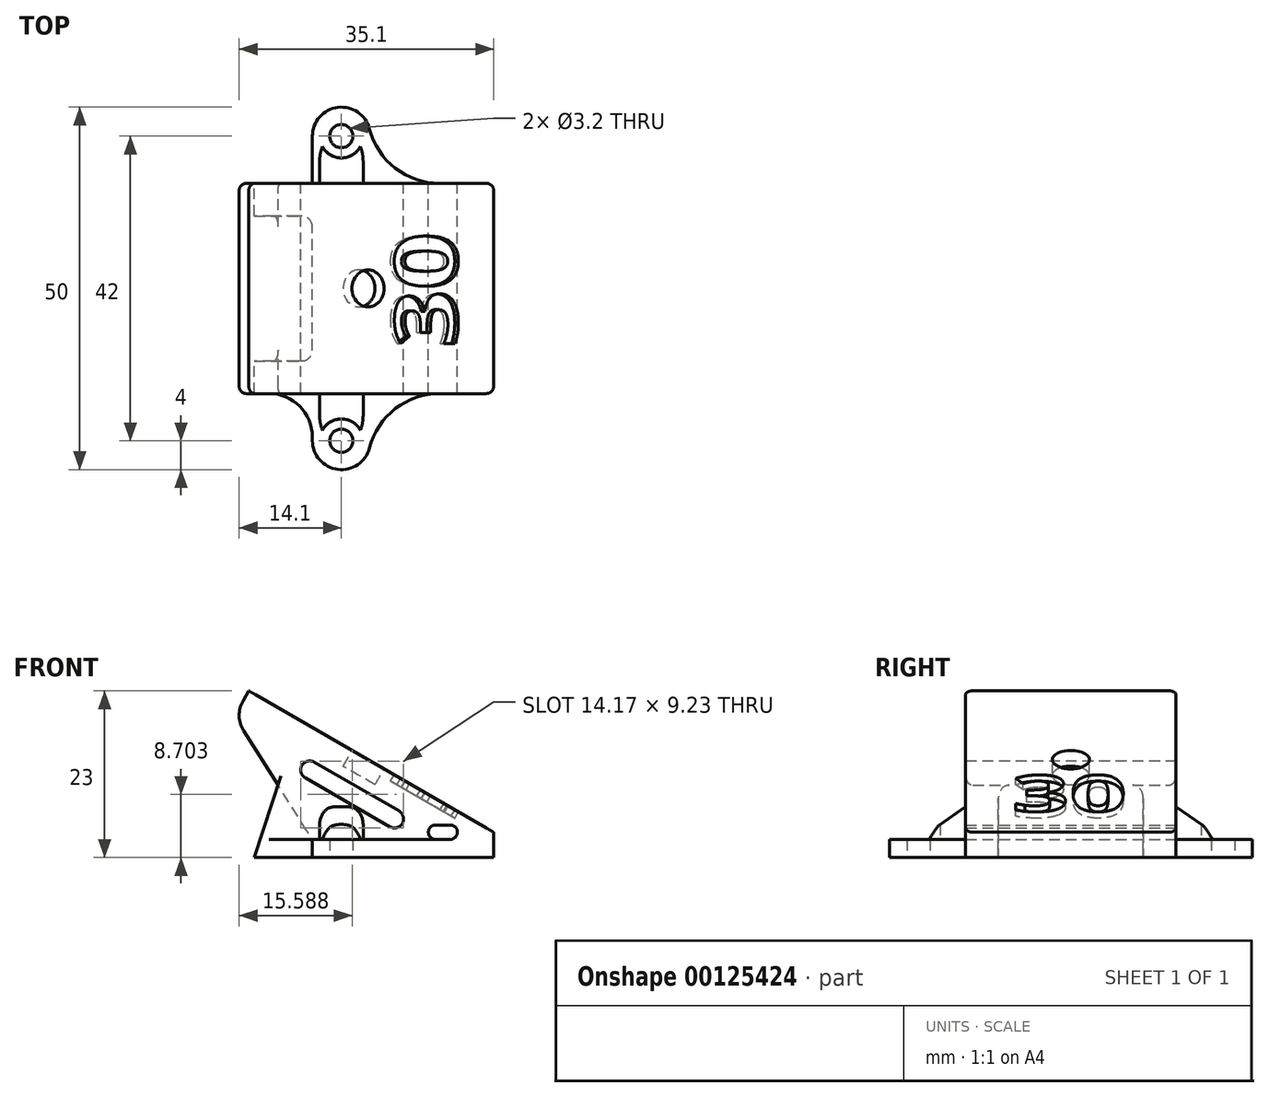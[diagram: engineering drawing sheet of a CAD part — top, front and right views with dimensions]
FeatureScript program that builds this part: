
annotation { "Feature Type Name" : "Feature", "Feature Type Description" : "" }
export const myFeature = defineFeature(function(context is Context, id is Id, definition is map)
    precondition{}
    {
        {
            var Q0;
            Q0=qCreatedBy(makeId("Front.planeOp"),FACE);
            var sketch = newSketch(context, id + "F0", { "sketchPlane" : qUnion([Q0])});
            skLineSegment(sketch, "E0", {"start": v(-33.77, 23) * mm, "end": v(0, 3.5) * mm});
            skLineSegment(sketch, "E1", {"start": v(-33.77, 23) * mm, "end": v(-34.57, 21.63) * mm});
            skLineSegment(sketch, "E2", {"start": v(-34.48, 17.5) * mm, "end": v(-25, 2.5) * mm});
            skLineSegment(sketch, "E3", {"start": v(0, 0) * mm, "end": v(0, 3.5) * mm});
            skLineSegment(sketch, "E4", {"start": v(-26.44, 12.7) * mm, "end": v(-26.44, 12.7) * mm});
            skLineSegment(sketch, "E5", {"start": v(-25.98, 11) * mm, "end": v(-14.3, 4.25) * mm});
            skLineSegment(sketch, "E6", {"start": v(-12.58, 4.7) * mm, "end": v(-12.58, 4.7) * mm});
            skLineSegment(sketch, "E7", {"start": v(-13.04, 6.41) * mm, "end": v(-24.73, 13.16) * mm});
            skLineSegment(sketch, "E8", {"start": v(-16.89, 13.25) * mm, "end": v(-18.89, 9.79) * mm, "construction": true});
            skPoint(sketch, "E9.visualSharp", {"position": v(-25.82, 13.79) * mm});
            skArc(sketch, "E9.filletArc", {"start": v(-24.73, 13.16) * mm, "mid": v(-25.68, 13.29) * mm, "end": v(-26.44, 12.7) * mm});
            skPoint(sketch, "E10.visualSharp", {"position": v(-11.96, 5.79) * mm});
            skArc(sketch, "E10.filletArc", {"start": v(-12.58, 4.7) * mm, "mid": v(-12.46, 5.65) * mm, "end": v(-13.04, 6.41) * mm});
            skPoint(sketch, "E11.visualSharp", {"position": v(-13.2, 3.62) * mm});
            skArc(sketch, "E11.filletArc", {"start": v(-14.3, 4.25) * mm, "mid": v(-13.34, 4.12) * mm, "end": v(-12.58, 4.7) * mm});
            skPoint(sketch, "E12.visualSharp", {"position": v(-27.07, 11.62) * mm});
            skArc(sketch, "E12.filletArc", {"start": v(-26.44, 12.7) * mm, "mid": v(-26.57, 11.75) * mm, "end": v(-25.98, 11) * mm});
            skLineSegment(sketch, "E13", {"start": v(-8, 3.5) * mm, "end": v(-6, 3.5) * mm, "construction": true});
            skArc(sketch, "E14.0.startCap", {"start": v(-8, 2.5) * mm, "mid": v(-9, 3.5) * mm, "end": v(-8, 4.5) * mm});
            skArc(sketch, "E14.0.endCap", {"start": v(-6, 4.5) * mm, "mid": v(-5, 3.5) * mm, "end": v(-6, 2.5) * mm});
            skLineSegment(sketch, "E14.0.left", {"start": v(-8, 4.5) * mm, "end": v(-6, 4.5) * mm});
            skLineSegment(sketch, "E14.0.right", {"start": v(-8, 2.5) * mm, "end": v(-6, 2.5) * mm});
            skPoint(sketch, "E15.visualSharp", {"position": v(-35.77, 19.54) * mm});
            skArc(sketch, "E15.filletArc", {"start": v(-34.57, 21.63) * mm, "mid": v(-35.1, 19.55) * mm, "end": v(-34.48, 17.5) * mm});
            skLineSegment(sketch, "E16", {"start": v(0, 0) * mm, "end": v(-25, 0) * mm});
            skLineSegment(sketch, "E17", {"start": v(-25, 2.5) * mm, "end": v(-25, 0) * mm});
            skSolve(sketch);
        }
        {
            var Q0;
            Q0=makeQuery(id+"F0.imprint","IMPRINT",FACE,{"disambiguationData":[TD([[makeQuery(id+"F0.imprint","IMPRINT",EDGE,{"derivedFrom":sQuery(id+"F0.wireOp",EDGE,"E0")}),-1.0]])]});
            extrude(context, id + "F1", {"entities" : qUnion([Q0]), "endBound" : BoundingType.SYMMETRIC, "depth" : 29 * mm, "offsetDistance" : 25 * mm});
        }
        {
            var Q0;
            Q0=makeQuery(id+"F1.opExtrude","SWEPT_FACE",FACE,{"disambiguationData":[OSD([sQuery(id+"F0.wireOp",EDGE,"E16")])]});
            var sketch = newSketch(context, id + "F2", { "sketchPlane" : qUnion([Q0])});
            skCircle(sketch, "E18", {"center": v(-21, 21) * mm, "radius": 1.6 * mm});
            skArc(sketch, "E19", {"start": v(-17.13, 22) * mm, "mid": v(-21.5, 24.97) * mm, "end": v(-25, 21) * mm});
            skCircle(sketch, "E20.MirrorC", {"center": v(-21, -21) * mm, "radius": 1.6 * mm});
            skLineSegment(sketch, "E21", {"start": v(-25, 21) * mm, "end": v(-25, -21) * mm});
            skArc(sketch, "E22", {"start": v(-17.13, 22) * mm, "mid": v(-13.57, 16.6) * mm, "end": v(-7.44, 14.5) * mm});
            skLineSegment(sketch, "E23", {"start": v(-7.44, 14.5) * mm, "end": v(-7.44, -14.5) * mm});
            skArc(sketch, "E24.MirrorCS", {"start": v(-17.13, -22) * mm, "mid": v(-21.5, -24.97) * mm, "end": v(-25, -21) * mm});
            skArc(sketch, "E25.MirrorCS", {"start": v(-17.13, -22) * mm, "mid": v(-13.57, -16.6) * mm, "end": v(-7.44, -14.5) * mm});
            skSolve(sketch);
        }
        {
            var Q0;
            Q0=qSketchRegion(id+"F2",true);
            extrude(context, id + "F3", {"entities" : qUnion([Q0]), "operationType" : NewBodyOperationType.ADD, "oppositeDirection" : true, "depth" : 2.5 * mm, "offsetDistance" : 25 * mm});
        }
        {
            var Q0;
            {var subQ4=sQuery(id+"F2.wireOp",EDGE,"E21");var subQ6=sQuery(id+"F2.wireOp",EDGE,"E19");Q0=makeQuery(id+"Fg2Gqv11Pvh0zDd_1.boolean.opBoolean","SPLIT",FACE,{"disambiguationData":[TD([makeQuery(id+"F3.opExtrude","SWEPT_FACE",FACE,{"disambiguationData":[OSD([subQ6])]})])],"derivedFrom":makeQuery(id+"F3.boolean.opBoolean","MERGE",FACE,{"derivedFrom":[makeQuery(id+"F1.opExtrude","SWEPT_FACE",FACE,{"disambiguationData":[OSD([sQuery(id+"F0.wireOp",EDGE,"E17")])]}),makeQuery(id+"F3.opExtrude","SWEPT_FACE",FACE,{"disambiguationData":[OSD([subQ4])]})]})});}
            var sketch = newSketch(context, id + "F4", { "sketchPlane" : qUnion([Q0])});
            skLineSegment(sketch, "E26", {"start": v(-21, 2.5) * mm, "end": v(-14.5, 7) * mm});
            skLineSegment(sketch, "E27", {"start": v(-14.5, 7) * mm, "end": v(-14.5, 2.5) * mm});
            skLineSegment(sketch, "E28", {"start": v(-14.5, 2.5) * mm, "end": v(-21, 2.5) * mm});
            skSolve(sketch);
        }
        {
            var Q0;
            Q0=makeQuery(id+"F4.imprint","IMPRINT",FACE,{"disambiguationData":[TD([[makeQuery(id+"F4.imprint","IMPRINT",EDGE,{"derivedFrom":sQuery(id+"F4.wireOp",EDGE,"E26")}),-1.0]])]});
            extrude(context, id + "F5", {"entities" : qUnion([Q0]), "oppositeDirection" : true, "depth" : 7 * mm, "offsetDistance" : 25 * mm, "hasSecondDirection" : true, "secondDirectionOppositeDirection" : true, "secondDirectionDepth" : 1 * mm});
        }
        {
            var Q0;
            Q0=makeQuery(id+"F5.opExtrude","SWEPT_BODY",BODY,{"disambiguationData":[OSD([sQuery(id+"F4.wireOp",EDGE,"E26"),sQuery(id+"F4.wireOp",EDGE,"E27"),sQuery(id+"F4.wireOp",EDGE,"E28")])]});
            var Q1;
            Q1=qCreatedBy(makeId("Front.planeOp"),FACE);
            mirror(context, id + "F6", {"operationType" : NewBodyOperationType.ADD, "entities" : qUnion([Q0]), "mirrorPlane" : qUnion([Q1])});
        }
        {
            var Q0;
            {var subQ0=sQuery(id+"F2.wireOp",EDGE,"E20.MirrorC");var subQ2=sQuery(id+"F2.wireOp",EDGE,"E21");var subQ4=sQuery(id+"F2.wireOp",EDGE,"E24.MirrorCS");var subQ5=sQuery(id+"F2.wireOp",EDGE,"E25.MirrorCS");Q0=makeQuery(id+"F3.boolean.opBoolean","SPLIT",FACE,{"disambiguationData":[TD([makeQuery(id+"F3.opExtrude","SWEPT_FACE",FACE,{"disambiguationData":[OSD([subQ0])]})])],"derivedFrom":makeQuery(id+"F3.opExtrude","CAP_FACE",FACE,{"disambiguationData":[OSD([sQuery(id+"F2.wireOp",EDGE,"E18"),sQuery(id+"F2.wireOp",EDGE,"E19"),subQ0,subQ2,sQuery(id+"F2.wireOp",EDGE,"E22"),sQuery(id+"F2.wireOp",EDGE,"E23"),subQ4,subQ5])],"isStart":false})});}
            var sketch = newSketch(context, id + "F7", { "sketchPlane" : qUnion([Q0])});
            skCircle(sketch, "E29", {"center": v(-21, 21) * mm, "radius": 3 * mm});
            skCircle(sketch, "E30", {"center": v(-21, -21) * mm, "radius": 3 * mm});
            skSolve(sketch);
        }
        {
            var Q0;
            Q0=makeQuery(id+"F5.opExtrude","CAP_EDGE",EDGE,{"disambiguationData":[OSD([sQuery(id+"F4.wireOp",EDGE,"E26")])],"isStart":true});
            var Q1;
            Q1=makeQuery(id+"F5.opExtrude","CAP_EDGE",EDGE,{"disambiguationData":[OSD([sQuery(id+"F4.wireOp",EDGE,"E26")])],"isStart":false});
            var Q2;
            Q2=makeQuery(id+"F6.opPattern","COPY",EDGE,{"derivedFrom":makeQuery(id+"F5.opExtrude","CAP_EDGE",EDGE,{"disambiguationData":[OSD([sQuery(id+"F4.wireOp",EDGE,"E26")])],"isStart":true}),"instanceName":"1"});
            var Q3;
            Q3=makeQuery(id+"F6.opPattern","COPY",EDGE,{"derivedFrom":makeQuery(id+"F5.opExtrude","CAP_EDGE",EDGE,{"disambiguationData":[OSD([sQuery(id+"F4.wireOp",EDGE,"E26")])],"isStart":false}),"instanceName":"1"});
            fillet(context, id + "F8", {"entities" : qUnion([Q0, Q1, Q2, Q3]), "radius" : 2 * mm, "tangentPropagation" : true, "allowEdgeOverflow" : false});
        }
        {
            var Q0;
            Q0=qSketchRegion(id+"F7",true);
            extrude(context, id + "F9", {"entities" : qUnion([Q0]), "operationType" : NewBodyOperationType.REMOVE, "depth" : 25 * mm, "offsetDistance" : 25 * mm});
        }
        {
            var Q0;
            Q0=makeQuery(id+"F1.opExtrude","SWEPT_FACE",FACE,{"disambiguationData":[OSD([sQuery(id+"F0.wireOp",EDGE,"E0")])]});
            var sketch = newSketch(context, id + "F10", { "sketchPlane" : qUnion([Q0])});
            skCircle(sketch, "E31", {"center": v(-21.75, 0) * mm, "radius": 2.55 * mm});
            skLineSegment(sketch, "E32", {"start": v(-21.75, 0) * mm, "end": v(0, 0) * mm, "construction": true});
            skText(sketch, "E33", { "text": "30", "fontName": "OpenSans-Bold.ttf"});
            const initialGuessF10  = {"E33": [-0.0075, -0.00813, 0, 1, 0.01]};
            skSetInitialGuess(sketch, initialGuessF10);
            skSolve(sketch);
        }
        {
            var Q0;
            Q0=makeQuery(id+"F10.imprint","IMPRINT",FACE,{"disambiguationData":[TD([[makeQuery(id+"F10.imprint","IMPRINT",EDGE,{"derivedFrom":sQuery(id+"F10.wireOp",EDGE,"E31")}),1.0]])]});
            extrude(context, id + "F11", {"entities" : qUnion([Q0]), "operationType" : NewBodyOperationType.REMOVE, "depth" : -2.5 * mm, "offsetDistance" : 25 * mm});
        }
        {
            var Q0;
            Q0=makeQuery(id+"F10.imprint","IMPRINT",FACE,{"disambiguationData":[TD([[makeQuery(id+"F10.imprint","IMPRINT",EDGE,{"derivedFrom":sQuery(id+"F10.wireOp",EDGE,"E33.sketch_text.stroke-0")}),-1.0]])]});
            var Q1;
            Q1=makeQuery(id+"F10.imprint","IMPRINT",FACE,{"disambiguationData":[TD([[makeQuery(id+"F10.imprint","IMPRINT",EDGE,{"derivedFrom":sQuery(id+"F10.wireOp",EDGE,"E33.sketch_text.stroke-27")}),-1.0]])]});
            extrude(context, id + "F12", {"entities" : qUnion([Q0, Q1]), "operationType" : NewBodyOperationType.REMOVE, "oppositeDirection" : true, "depth" : 1 * mm, "offsetDistance" : 25 * mm});
        }
        {
            var Q0;
            Q0=qCreatedBy(makeId("Front.planeOp"),FACE);
            var sketch = newSketch(context, id + "F13", { "sketchPlane" : qUnion([Q0])});
            skLineSegment(sketch, "E34", {"start": v(-29.74, 10) * mm, "end": v(-33, 0) * mm});
            skLineSegment(sketch, "E35", {"start": v(-33, 0) * mm, "end": v(-25, 0) * mm});
            skLineSegment(sketch, "E36", {"start": v(-25, 0) * mm, "end": v(-25, 2.5) * mm});
            skLineSegment(sketch, "E37", {"start": v(-25, 2.5) * mm, "end": v(-29.74, 10) * mm});
            skSolve(sketch);
        }
        {
            var Q0;
            Q0=makeQuery(id+"F13.imprint","IMPRINT",FACE,{"disambiguationData":[TD([[makeQuery(id+"F13.imprint","IMPRINT",EDGE,{"derivedFrom":sQuery(id+"F13.wireOp",EDGE,"E34")}),1.0]])]});
            extrude(context, id + "F14", {"entities" : qUnion([Q0]), "operationType" : NewBodyOperationType.ADD, "endBound" : BoundingType.SYMMETRIC, "depth" : 29 * mm, "offsetDistance" : 25 * mm});
        }
        {
            var Q0;
            Q0 = qSketchRegion(id + "F13", true);
            extrude(context, id + "F15", {"entities" : qUnion([Q0]), "operationType" : NewBodyOperationType.REMOVE, "endBound" : BoundingType.SYMMETRIC, "depth" : 20 * mm, "offsetDistance" : 25 * mm});
        }
        {
            var Q0;
            Q0=makeQuery(id+"F15.boolean.opBoolean","COPY",EDGE,{"derivedFrom":makeQuery(id+"F15.opExtrude","SWEPT_EDGE",EDGE,{"disambiguationData":[OSD([sQuery(id+"F13.wireOp",EDGE,"E36"),sQuery(id+"F13.wireOp",EDGE,"E37")])]})});
            var Q1;
            {var subQ0=sQuery(id+"F13.wireOp",EDGE,"E37");var subQ1=sQuery(id+"F13.wireOp",EDGE,"E36");var subQ2=sQuery(id+"F13.wireOp",EDGE,"E35");var subQ3=sQuery(id+"F13.wireOp",EDGE,"E34");Q1=makeQuery(id+"F15.boolean.opBoolean","SPLIT",EDGE,{"disambiguationData":[TD([makeQuery(id+"F14.opExtrude","CAP_FACE",FACE,{"disambiguationData":[OSD([subQ3,subQ2,subQ1,subQ0])],"isStart":true})])],"derivedFrom":makeQuery(id+"F14.opExtrude","SWEPT_EDGE",EDGE,{"disambiguationData":[OSD([subQ3,subQ0])]})});}
            var Q2;
            {var subQ0=sQuery(id+"F13.wireOp",EDGE,"E37");var subQ1=sQuery(id+"F13.wireOp",EDGE,"E36");var subQ2=sQuery(id+"F13.wireOp",EDGE,"E35");var subQ3=sQuery(id+"F13.wireOp",EDGE,"E34");Q2=makeQuery(id+"F15.boolean.opBoolean","SPLIT",EDGE,{"disambiguationData":[TD([makeQuery(id+"F14.opExtrude","CAP_FACE",FACE,{"disambiguationData":[OSD([subQ3,subQ2,subQ1,subQ0])],"isStart":false})])],"derivedFrom":makeQuery(id+"F14.opExtrude","SWEPT_EDGE",EDGE,{"disambiguationData":[OSD([subQ3,subQ0])]})});}
            fillet(context, id + "F16", {"entities" : qUnion([Q0, Q1, Q2]), "radius" : 5 * mm, "tangentPropagation" : true, "allowEdgeOverflow" : false});
        }
        {
            var Q0;
            Q0=makeQuery(id+"F15.boolean.opBoolean","COPY",EDGE,{"derivedFrom":makeQuery(id+"F15.opExtrude","CAP_EDGE",EDGE,{"disambiguationData":[OSD([sQuery(id+"F13.wireOp",EDGE,"E37")])],"isStart":true})});
            var Q1;
            Q1=makeQuery(id+"F15.boolean.opBoolean","COPY",EDGE,{"derivedFrom":makeQuery(id+"F15.opExtrude","CAP_EDGE",EDGE,{"disambiguationData":[OSD([sQuery(id+"F13.wireOp",EDGE,"E37")])],"isStart":false})});
            fillet(context, id + "F17", {"entities" : qUnion([Q0, Q1]), "radius" : 1.5 * mm, "tangentPropagation" : true, "allowEdgeOverflow" : false});
        }
        {
            var Q0;
            Q0=makeQuery(id+"F1.opExtrude","CAP_EDGE",EDGE,{"disambiguationData":[OSD([sQuery(id+"F0.wireOp",EDGE,"E1")])],"isStart":true});
            var Q1;
            Q1=makeQuery(id+"F1.opExtrude","CAP_EDGE",EDGE,{"disambiguationData":[OSD([sQuery(id+"F0.wireOp",EDGE,"E1")])],"isStart":false});
            var Q2;
            {var subQ0=sQuery(id+"F13.wireOp",EDGE,"E37");var subQ1=sQuery(id+"F13.wireOp",EDGE,"E36");var subQ2=sQuery(id+"F13.wireOp",EDGE,"E35");var subQ3=sQuery(id+"F13.wireOp",EDGE,"E34");Q2=makeQuery(id+"F17.opFillet","BLEND_EDGE",EDGE,{"blendedFrom":[makeQuery(id+"F15.boolean.opBoolean","COPY",EDGE,{"derivedFrom":makeQuery(id+"F15.opExtrude","CAP_EDGE",EDGE,{"disambiguationData":[OSD([subQ0])],"isStart":false})}),makeQuery(id+"F16.opFillet","BLEND_FACE",FACE,{"disambiguationData":[OSD([subQ3,subQ0]),TDD([makeQuery(id+"F15.boolean.opBoolean","SPLIT",EDGE,{"disambiguationData":[TD([makeQuery(id+"F14.opExtrude","CAP_FACE",FACE,{"disambiguationData":[OSD([subQ3,subQ2,subQ1,subQ0])],"isStart":false})])],"derivedFrom":makeQuery(id+"F14.opExtrude","SWEPT_EDGE",EDGE,{"disambiguationData":[OSD([subQ3,subQ0])]})})])]})],"blendedInto":[makeQuery(id+"F16.opFillet","BLEND_FACE",FACE,{"disambiguationData":[OSD([subQ3,subQ0]),TDD([makeQuery(id+"F15.boolean.opBoolean","SPLIT",EDGE,{"disambiguationData":[TD([makeQuery(id+"F14.opExtrude","CAP_FACE",FACE,{"disambiguationData":[OSD([subQ3,subQ2,subQ1,subQ0])],"isStart":false})])],"derivedFrom":makeQuery(id+"F14.opExtrude","SWEPT_EDGE",EDGE,{"disambiguationData":[OSD([subQ3,subQ0])]})})])]})]});}
            var Q3;
            {var subQ0=sQuery(id+"F13.wireOp",EDGE,"E37");var subQ1=sQuery(id+"F13.wireOp",EDGE,"E36");var subQ2=sQuery(id+"F13.wireOp",EDGE,"E35");var subQ3=sQuery(id+"F13.wireOp",EDGE,"E34");Q3=makeQuery(id+"F17.opFillet","BLEND_EDGE",EDGE,{"blendedFrom":[makeQuery(id+"F15.boolean.opBoolean","COPY",EDGE,{"derivedFrom":makeQuery(id+"F15.opExtrude","CAP_EDGE",EDGE,{"disambiguationData":[OSD([subQ0])],"isStart":true})}),makeQuery(id+"F16.opFillet","BLEND_FACE",FACE,{"disambiguationData":[OSD([subQ3,subQ0]),TDD([makeQuery(id+"F15.boolean.opBoolean","SPLIT",EDGE,{"disambiguationData":[TD([makeQuery(id+"F14.opExtrude","CAP_FACE",FACE,{"disambiguationData":[OSD([subQ3,subQ2,subQ1,subQ0])],"isStart":true})])],"derivedFrom":makeQuery(id+"F14.opExtrude","SWEPT_EDGE",EDGE,{"disambiguationData":[OSD([subQ3,subQ0])]})})])]})],"blendedInto":[makeQuery(id+"F16.opFillet","BLEND_FACE",FACE,{"disambiguationData":[OSD([subQ3,subQ0]),TDD([makeQuery(id+"F15.boolean.opBoolean","SPLIT",EDGE,{"disambiguationData":[TD([makeQuery(id+"F14.opExtrude","CAP_FACE",FACE,{"disambiguationData":[OSD([subQ3,subQ2,subQ1,subQ0])],"isStart":true})])],"derivedFrom":makeQuery(id+"F14.opExtrude","SWEPT_EDGE",EDGE,{"disambiguationData":[OSD([subQ3,subQ0])]})})])]})]});}
            var Q4;
            Q4=makeQuery(id+"F1.opExtrude","CAP_EDGE",EDGE,{"disambiguationData":[OSD([sQuery(id+"F0.wireOp",EDGE,"E3")])],"isStart":false});
            var Q5;
            Q5=makeQuery(id+"F1.opExtrude","CAP_EDGE",EDGE,{"disambiguationData":[OSD([sQuery(id+"F0.wireOp",EDGE,"E3")])],"isStart":true});
            fillet(context, id + "F18", {"entities" : qUnion([Q0, Q1, Q2, Q3, Q4, Q5]), "radius" : 1 * mm, "tangentPropagation" : true, "allowEdgeOverflow" : false});
        }
        {
            var Q0;
            Q0=makeQuery(id+"F14.opExtrude","CAP_EDGE",EDGE,{"disambiguationData":[OSD([sQuery(id+"F13.wireOp",EDGE,"E36")])],"isStart":true});
            var Q1;
            Q1=makeQuery(id+"F14.opExtrude","CAP_EDGE",EDGE,{"disambiguationData":[OSD([sQuery(id+"F13.wireOp",EDGE,"E36")])],"isStart":false});
            fillet(context, id + "F19", {"entities" : qUnion([Q0, Q1]), "radius" : 6 * mm, "tangentPropagation" : true, "allowEdgeOverflow" : false});
        }
    });
